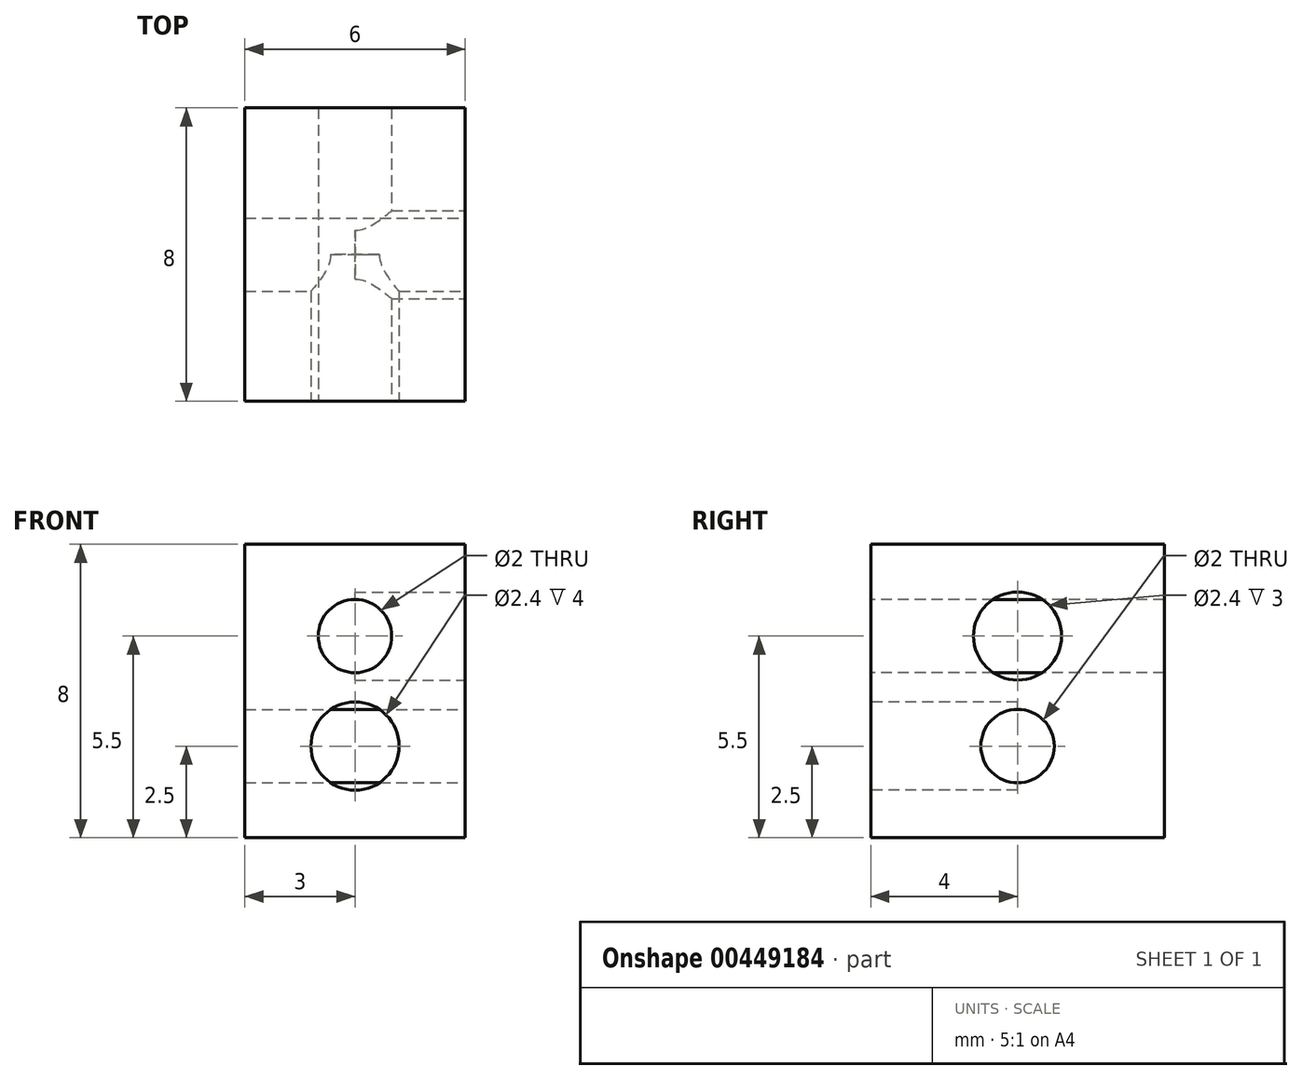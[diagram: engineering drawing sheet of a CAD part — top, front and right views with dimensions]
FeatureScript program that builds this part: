
annotation { "Feature Type Name" : "Feature", "Feature Type Description" : "" }
export const myFeature = defineFeature(function(context is Context, id is Id, definition is map)
    precondition{}
    {
        {
            var Q0;
            Q0=qCreatedBy(makeId("Front.planeOp"),FACE);
            var sketch = newSketch(context, id + "F0", { "sketchPlane" : qUnion([Q0])});
            skLineSegment(sketch, "E0.bottom", {"start": v(3, 4) * mm, "end": v(-3, 4) * mm});
            skLineSegment(sketch, "E0.top", {"start": v(3, -4) * mm, "end": v(-3, -4) * mm});
            skLineSegment(sketch, "E0.left", {"start": v(3, 4) * mm, "end": v(3, -4) * mm});
            skLineSegment(sketch, "E0.right", {"start": v(-3, 4) * mm, "end": v(-3, -4) * mm});
            skPoint(sketch, "E0.middle", {"position": v(0, 0) * mm});
            skSolve(sketch);
        }
        {
            var Q0;
            Q0 = qSketchRegion(id + "F0", true);
            extrude(context, id + "F1", {"entities" : qUnion([Q0]), "depth" : 4 * mm, "hasSecondDirection" : true, "secondDirectionOppositeDirection" : true, "secondDirectionDepth" : 4 * mm});
        }
        {
            var Q0;
            Q0=makeQuery(id+"F1.opExtrude","CAP_FACE",FACE,{"disambiguationData":[OSD([sQuery(id+"F0.wireOp",EDGE,"E0.bottom"),sQuery(id+"F0.wireOp",EDGE,"E0.top"),sQuery(id+"F0.wireOp",EDGE,"E0.left"),sQuery(id+"F0.wireOp",EDGE,"E0.right")])],"isStart":false});
            var sketch = newSketch(context, id + "F2", { "sketchPlane" : qUnion([Q0])});
            skCircle(sketch, "E1", {"center": v(0, 1.5) * mm, "radius": 1 * mm});
            skSolve(sketch);
        }
        {
            var Q0;
            Q0 = qSketchRegion(id + "F2", true);
            extrude(context, id + "F3", {"entities" : qUnion([Q0]), "operationType" : NewBodyOperationType.REMOVE, "endBound" : BoundingType.THROUGH_ALL, "oppositeDirection" : true, "depth" : 25 * mm});
        }
        {
            var Q0;
            Q0=makeQuery(id+"F1.opExtrude","SWEPT_FACE",FACE,{"disambiguationData":[OSD([sQuery(id+"F0.wireOp",EDGE,"E0.left")])]});
            var sketch = newSketch(context, id + "F4", { "sketchPlane" : qUnion([Q0])});
            skCircle(sketch, "E2", {"center": v(0, -1.5) * mm, "radius": 1 * mm});
            skSolve(sketch);
        }
        {
            var Q0;
            Q0 = qSketchRegion(id + "F4", true);
            extrude(context, id + "F5", {"entities" : qUnion([Q0]), "operationType" : NewBodyOperationType.REMOVE, "endBound" : BoundingType.THROUGH_ALL, "oppositeDirection" : true, "depth" : 25 * mm});
        }
        {
            var Q0;
            Q0=makeQuery(id+"F1.opExtrude","CAP_FACE",FACE,{"disambiguationData":[OSD([sQuery(id+"F0.wireOp",EDGE,"E0.bottom"),sQuery(id+"F0.wireOp",EDGE,"E0.top"),sQuery(id+"F0.wireOp",EDGE,"E0.left"),sQuery(id+"F0.wireOp",EDGE,"E0.right")])],"isStart":false});
            var sketch = newSketch(context, id + "F6", { "sketchPlane" : qUnion([Q0])});
            skCircle(sketch, "E3", {"center": v(0, -1.5) * mm, "radius": 1.2 * mm});
            skSolve(sketch);
        }
        {
            var Q0;
            Q0 = qSketchRegion(id + "F6", true);
            extrude(context, id + "F7", {"entities" : qUnion([Q0]), "operationType" : NewBodyOperationType.REMOVE, "oppositeDirection" : true, "depth" : 4 * mm});
        }
        {
            var Q0;
            Q0=makeQuery(id+"F1.opExtrude","SWEPT_FACE",FACE,{"disambiguationData":[OSD([sQuery(id+"F0.wireOp",EDGE,"E0.left")])]});
            var sketch = newSketch(context, id + "F8", { "sketchPlane" : qUnion([Q0])});
            skCircle(sketch, "E4", {"center": v(0, 1.5) * mm, "radius": 1.2 * mm});
            skSolve(sketch);
        }
        {
            var Q0;
            Q0 = qSketchRegion(id + "F8", true);
            extrude(context, id + "F9", {"entities" : qUnion([Q0]), "operationType" : NewBodyOperationType.REMOVE, "oppositeDirection" : true, "depth" : 3 * mm});
        }
    });
